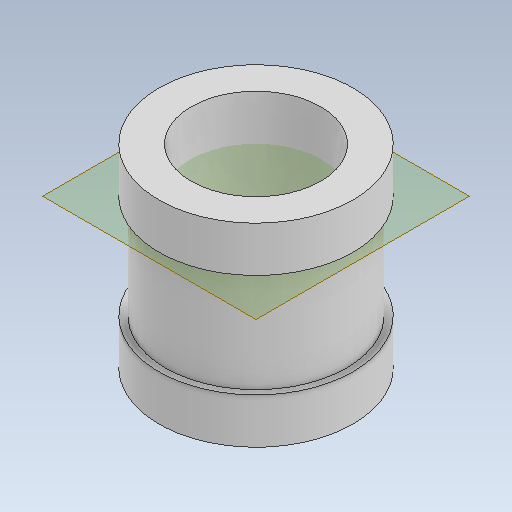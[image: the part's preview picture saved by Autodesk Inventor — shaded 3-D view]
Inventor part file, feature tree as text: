
AUTODESK INVENTOR PART (.ipt)
format: ipt  version: 2023 (Build 270158000, 158)  size: 120,320 bytes
history: native  units: mm
features: other x3, sketch x2, plane x1
ambient origin geometry x8: Origin, YZ Plane, XZ Plane, XY Plane, X Axis, Y Axis, Z Axis, Center Point
bodies: Solid1 (feature_tree)
feature tree (6):
  other  "screw_holder_2_3.ipt"
  other  "Solid1::screw_holder_2_3.ipt"
  other  "TaggingFeature1"
  sketch  "Sketch1"  dims[d0=10.0mm]
  sketch  "Sketch2"
  plane  "Work Plane1"
